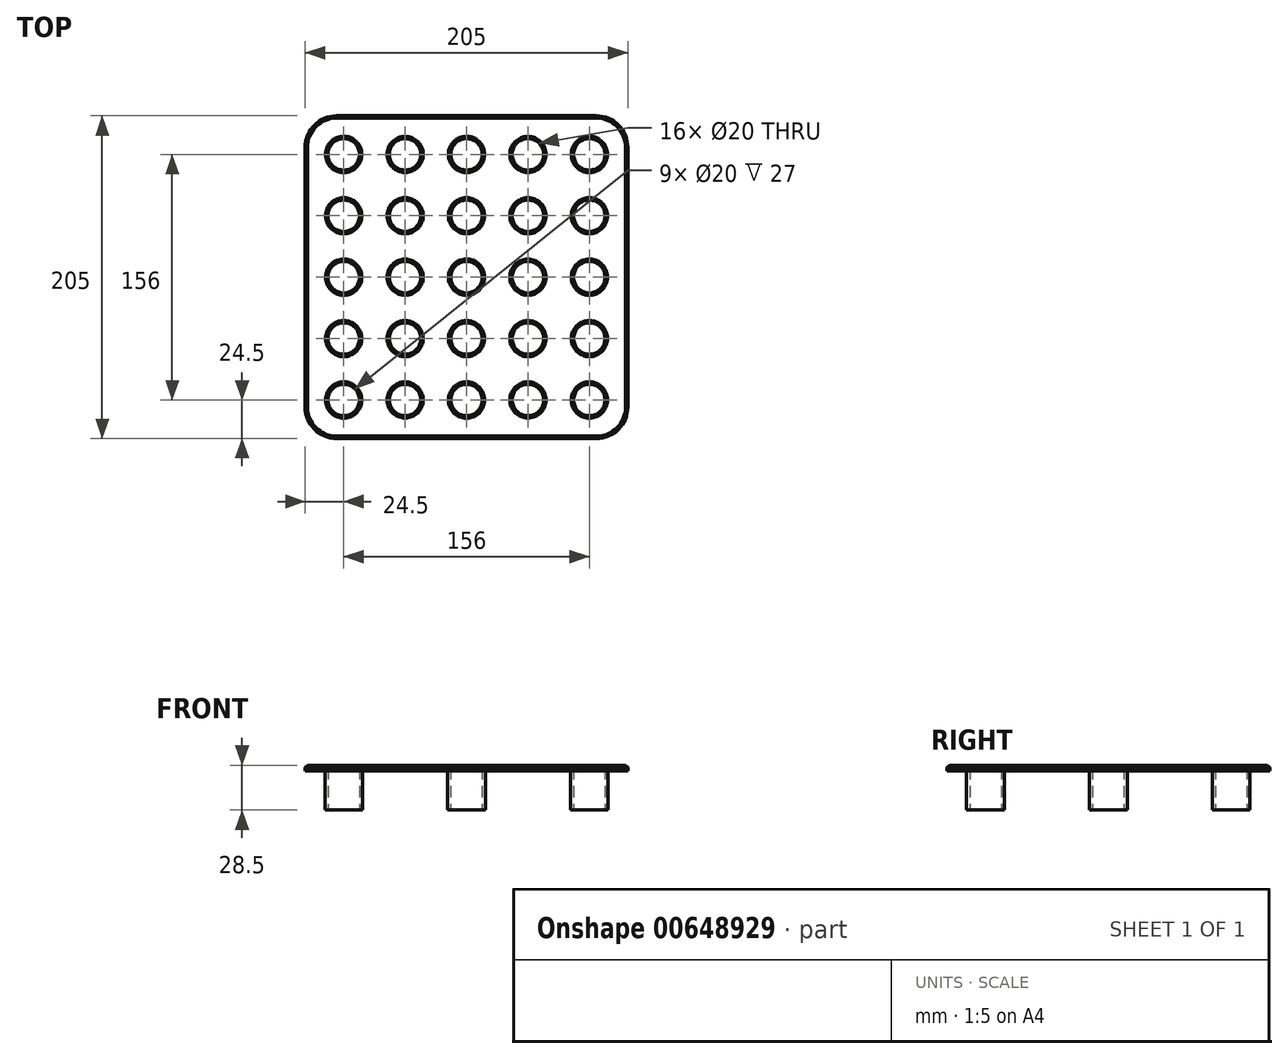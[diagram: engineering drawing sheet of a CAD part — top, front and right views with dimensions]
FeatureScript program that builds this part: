
annotation { "Feature Type Name" : "Feature", "Feature Type Description" : "" }
export const myFeature = defineFeature(function(context is Context, id is Id, definition is map)
    precondition{}
    {
        {
            var Q0;
            Q0=qCreatedBy(makeId("Top.planeOp"),FACE);
            var sketch = newSketch(context, id + "F0", { "sketchPlane" : qUnion([Q0])});
            skLineSegment(sketch, "E0.bottom", {"start": v(82.5, 102.5) * mm, "end": v(-82.5, 102.5) * mm});
            skLineSegment(sketch, "E0.top", {"start": v(82.5, -102.5) * mm, "end": v(-82.5, -102.5) * mm});
            skLineSegment(sketch, "E0.left", {"start": v(102.5, 82.5) * mm, "end": v(102.5, -82.5) * mm});
            skLineSegment(sketch, "E0.right", {"start": v(-102.5, 82.5) * mm, "end": v(-102.5, -82.5) * mm});
            skPoint(sketch, "E0.middle", {"position": v(0, 0) * mm});
            skPoint(sketch, "E1.visualSharp", {"position": v(102.5, 102.5) * mm});
            skArc(sketch, "E1.filletArc", {"start": v(102.5, 82.5) * mm, "mid": v(96.64, 96.64) * mm, "end": v(82.5, 102.5) * mm});
            skPoint(sketch, "E2.visualSharp", {"position": v(102.5, -102.5) * mm});
            skArc(sketch, "E2.filletArc", {"start": v(82.5, -102.5) * mm, "mid": v(96.64, -96.64) * mm, "end": v(102.5, -82.5) * mm});
            skPoint(sketch, "E3.visualSharp", {"position": v(-102.5, -102.5) * mm});
            skArc(sketch, "E3.filletArc", {"start": v(-102.5, -82.5) * mm, "mid": v(-96.64, -96.64) * mm, "end": v(-82.5, -102.5) * mm});
            skPoint(sketch, "E4.visualSharp", {"position": v(-102.5, 102.5) * mm});
            skArc(sketch, "E4.filletArc", {"start": v(-82.5, 102.5) * mm, "mid": v(-96.64, 96.64) * mm, "end": v(-102.5, 82.5) * mm});
            skSolve(sketch);
        }
        {
            var Q0;
            Q0 = qSketchRegion(id + "F0", true);
            extrude(context, id + "F1", {"entities" : qUnion([Q0]), "depth" : 3.5 * mm, "offsetDistance" : 25 * mm});
        }
        {
            var Q0;
            Q0=qCreatedBy(makeId("Top.planeOp"),FACE);
            var sketch = newSketch(context, id + "F2", { "sketchPlane" : qUnion([Q0])});
            skCircle(sketch, "E5", {"center": v(-78, 78) * mm, "radius": 10 * mm});
            skLineSegment(sketch, "E6", {"start": v(-78, 78) * mm, "end": v(0, 0) * mm, "construction": true});
            skCircle(sketch, "E7.0.1.0", {"center": v(-78, 39) * mm, "radius": 10 * mm});
            skCircle(sketch, "E7.0.2.0", {"center": v(-78, 0) * mm, "radius": 10 * mm});
            skCircle(sketch, "E7.0.3.0", {"center": v(-78, -39) * mm, "radius": 10 * mm});
            skCircle(sketch, "E7.0.4.0", {"center": v(-78, -78) * mm, "radius": 10 * mm});
            skCircle(sketch, "E7.1.0.0", {"center": v(-39, 78) * mm, "radius": 10 * mm});
            skCircle(sketch, "E7.1.1.0", {"center": v(-39, 39) * mm, "radius": 10 * mm});
            skCircle(sketch, "E7.1.2.0", {"center": v(-39, 0) * mm, "radius": 10 * mm});
            skCircle(sketch, "E7.1.3.0", {"center": v(-39, -39) * mm, "radius": 10 * mm});
            skCircle(sketch, "E7.1.4.0", {"center": v(-39, -78) * mm, "radius": 10 * mm});
            skCircle(sketch, "E7.2.0.0", {"center": v(0, 78) * mm, "radius": 10 * mm});
            skCircle(sketch, "E7.2.1.0", {"center": v(0, 39) * mm, "radius": 10 * mm});
            skCircle(sketch, "E7.2.2.0", {"center": v(0, 0) * mm, "radius": 10 * mm});
            skCircle(sketch, "E7.2.3.0", {"center": v(0, -39) * mm, "radius": 10 * mm});
            skCircle(sketch, "E7.2.4.0", {"center": v(0, -78) * mm, "radius": 10 * mm});
            skCircle(sketch, "E7.3.0.0", {"center": v(39, 78) * mm, "radius": 10 * mm});
            skCircle(sketch, "E7.3.1.0", {"center": v(39, 39) * mm, "radius": 10 * mm});
            skCircle(sketch, "E7.3.2.0", {"center": v(39, 0) * mm, "radius": 10 * mm});
            skCircle(sketch, "E7.3.3.0", {"center": v(39, -39) * mm, "radius": 10 * mm});
            skCircle(sketch, "E7.3.4.0", {"center": v(39, -78) * mm, "radius": 10 * mm});
            skCircle(sketch, "E7.4.0.0", {"center": v(78, 78) * mm, "radius": 10 * mm});
            skCircle(sketch, "E7.4.1.0", {"center": v(78, 39) * mm, "radius": 10 * mm});
            skCircle(sketch, "E7.4.2.0", {"center": v(78, 0) * mm, "radius": 10 * mm});
            skCircle(sketch, "E7.4.3.0", {"center": v(78, -39) * mm, "radius": 10 * mm});
            skCircle(sketch, "E7.4.4.0", {"center": v(78, -78) * mm, "radius": 10 * mm});
            skLineSegment(sketch, "E7.direction1", {"start": v(-78, 78) * mm, "end": v(-39, 78) * mm, "construction": true});
            skLineSegment(sketch, "E7.direction2", {"start": v(-78, 78) * mm, "end": v(-78, 39) * mm, "construction": true});
            skSolve(sketch);
        }
        {
            var Q0;
            Q0 = qSketchRegion(id + "F2", true);
            extrude(context, id + "F3", {"entities" : qUnion([Q0]), "operationType" : NewBodyOperationType.REMOVE, "endBound" : BoundingType.THROUGH_ALL, "depth" : 25 * mm, "offsetDistance" : 25 * mm});
        }
        {
            var Q0;
            Q0=makeQuery(id+"F1.opExtrude","CAP_FACE",FACE,{"disambiguationData":[OSD([sQuery(id+"F0.wireOp",EDGE,"E0.bottom"),sQuery(id+"F0.wireOp",EDGE,"E0.top"),sQuery(id+"F0.wireOp",EDGE,"E0.left"),sQuery(id+"F0.wireOp",EDGE,"E0.right"),sQuery(id+"F0.wireOp",EDGE,"E1.filletArc"),sQuery(id+"F0.wireOp",EDGE,"E2.filletArc"),sQuery(id+"F0.wireOp",EDGE,"E3.filletArc"),sQuery(id+"F0.wireOp",EDGE,"E4.filletArc")])],"isStart":true});
            var sketch = newSketch(context, id + "F4", { "sketchPlane" : qUnion([Q0])});
            skCircle(sketch, "E8.0", {"center": v(-78, -78) * mm, "radius": 10 * mm});
            skCircle(sketch, "E9.0", {"center": v(-78, -78) * mm, "radius": 12 * mm});
            skCircle(sketch, "E10.0.1.0", {"center": v(-78, 0) * mm, "radius": 12 * mm});
            skCircle(sketch, "E10.0.1.1", {"center": v(-78, 0) * mm, "radius": 10 * mm});
            skCircle(sketch, "E10.0.2.0", {"center": v(-78, 78) * mm, "radius": 12 * mm});
            skCircle(sketch, "E10.0.2.1", {"center": v(-78, 78) * mm, "radius": 10 * mm});
            skCircle(sketch, "E10.1.0.0", {"center": v(0, -78) * mm, "radius": 12 * mm});
            skCircle(sketch, "E10.1.0.1", {"center": v(0, -78) * mm, "radius": 10 * mm});
            skCircle(sketch, "E10.1.1.0", {"center": v(0, 0) * mm, "radius": 12 * mm});
            skCircle(sketch, "E10.1.1.1", {"center": v(0, 0) * mm, "radius": 10 * mm});
            skCircle(sketch, "E10.1.2.0", {"center": v(0, 78) * mm, "radius": 12 * mm});
            skCircle(sketch, "E10.1.2.1", {"center": v(0, 78) * mm, "radius": 10 * mm});
            skCircle(sketch, "E10.2.0.0", {"center": v(78, -78) * mm, "radius": 12 * mm});
            skCircle(sketch, "E10.2.0.1", {"center": v(78, -78) * mm, "radius": 10 * mm});
            skCircle(sketch, "E10.2.1.0", {"center": v(78, 0) * mm, "radius": 12 * mm});
            skCircle(sketch, "E10.2.1.1", {"center": v(78, 0) * mm, "radius": 10 * mm});
            skCircle(sketch, "E10.2.2.0", {"center": v(78, 78) * mm, "radius": 12 * mm});
            skCircle(sketch, "E10.2.2.1", {"center": v(78, 78) * mm, "radius": 10 * mm});
            skLineSegment(sketch, "E10.direction1", {"start": v(-78, -78) * mm, "end": v(0, -78) * mm, "construction": true});
            skLineSegment(sketch, "E10.direction2", {"start": v(-78, -78) * mm, "end": v(-78, 0) * mm, "construction": true});
            skSolve(sketch);
        }
        {
            var Q0;
            Q0 = qSketchRegion(id + "F4", true);
            extrude(context, id + "F5", {"entities" : qUnion([Q0]), "operationType" : NewBodyOperationType.ADD, "depth" : 25 * mm, "offsetDistance" : 25 * mm});
        }
        {
            var Q0;
            Q0=makeQuery(id+"F1.opExtrude","CAP_FACE",FACE,{"disambiguationData":[OSD([sQuery(id+"F0.wireOp",EDGE,"E0.bottom"),sQuery(id+"F0.wireOp",EDGE,"E0.top"),sQuery(id+"F0.wireOp",EDGE,"E0.left"),sQuery(id+"F0.wireOp",EDGE,"E0.right"),sQuery(id+"F0.wireOp",EDGE,"E1.filletArc"),sQuery(id+"F0.wireOp",EDGE,"E2.filletArc"),sQuery(id+"F0.wireOp",EDGE,"E3.filletArc"),sQuery(id+"F0.wireOp",EDGE,"E4.filletArc")])],"isStart":false});
            chamfer(context, id + "F6", {"entities" : qUnion([Q0]), "width" : 1.5 * mm, "tangentPropagation" : true});
        }
    });
